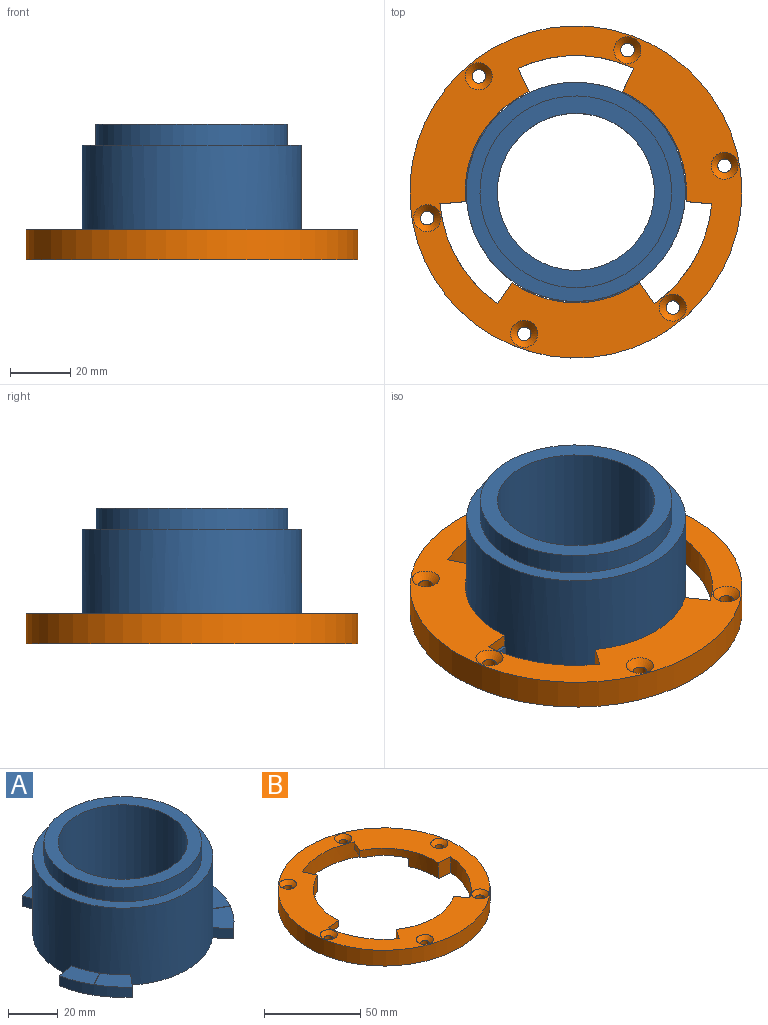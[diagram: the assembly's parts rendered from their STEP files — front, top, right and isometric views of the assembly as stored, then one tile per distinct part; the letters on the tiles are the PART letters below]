
ASSEMBLY  parts=2 mates=1
PART A: 24 faces, bbox 88.2x81.1x45 mm
  f0: cylinder r=36.3mm len=72.6mm, axis (0,0,-1), area 8278.7mm2, adj f4,f5,f9,f10,f11,f12,f13,f14
  f1: cylinder r=44.8mm len=26.54mm, axis (0,0,-1), area 160.6mm2, adj f4,f12,f14,f18,f19,f20
  f2: cylinder r=44.8mm len=30.65mm, axis (0,0,-1), area 160.6mm2, adj f4,f9,f11,f15,f16,f17
  f3: cylinder r=44.8mm len=26.54mm, axis (0,0,-1), area 160.6mm2, adj f4,f10,f13,f21,f22,f23
  f4: plane 88.24x81.1mm, normal (0,0,-1), area 2737.8mm2, adj f0,f1,f2,f3,f6,f9,f10,f11
  f5: plane 72.6x72.6mm, normal (0,0,1), area 972.7mm2, adj f0,f7
  f6: cylinder r=26mm len=52mm, axis (0,0,-1), area 7351.3mm2, adj f4,f8
  f7: cylinder r=31.75mm len=63.5mm, axis (0,0,-1), area 1396.4mm2, adj f5,f8
  f8: plane 63.5x63.5mm, normal (0,0,1), area 1043.2mm2, adj f6,f7
  f9: plane 7.99x5mm, normal (-0.94,-0.34,0), area 42.5mm2, adj f0,f2,f4,f15
  f10: plane 8.37x5mm, normal (-0.17,0.98,0), area 42.5mm2, adj f0,f3,f4,f22
  f11: plane 7.99x5mm, normal (0.94,-0.34,0), area 42.5mm2, adj f0,f2,f4,f16
  f12: plane 8.37x5mm, normal (0.17,0.98,0), area 42.5mm2, adj f0,f1,f4,f18
  f13: plane 6.51x5.46mm, normal (0.77,-0.64,0), area 42.5mm2, adj f0,f3,f4,f21
  f14: plane 6.51x5.46mm, normal (-0.77,-0.64,0), area 42.5mm2, adj f0,f1,f4,f19
  f15: plane 15.16x10.69mm, normal (-0.02,-0.01,1), area 118.9mm2, adj f0,f2,f9,f17
  f16: plane 15.16x10.69mm, normal (0.02,-0.01,1), area 118.9mm2, adj f0,f2,f11,f17
  f17: cylinder r=10mm len=8.5mm, axis (0,1,0.01), area 2.8mm2, adj f0,f2,f15,f16
  f18: plane 15.96x12.61mm, normal (0,0.02,1), area 118.9mm2, adj f0,f1,f12,f20
  f19: plane 16.03x15.39mm, normal (-0.01,-0.01,1), area 118.9mm2, adj f0,f1,f14,f20
  f20: cylinder r=10mm len=7.53mm, axis (-0.87,0.5,-0.01), area 2.8mm2, adj f0,f1,f18,f19
  f21: plane 16.03x15.39mm, normal (0.01,-0.01,1), area 118.9mm2, adj f0,f3,f13,f23
  f22: plane 15.96x12.61mm, normal (0,0.02,1), area 118.9mm2, adj f0,f3,f10,f23
  f23: cylinder r=10mm len=7.53mm, axis (0.87,0.5,-0.01), area 2.8mm2, adj f0,f3,f21,f22
PART B: 39 faces, bbox 110x110x10 mm
  f0: plane 110x110mm, normal (0,0,-1), area 3536.2mm2, adj f4,f5,f6,f8,f9,f10,f11,f12
  f1: plane 8.47x4mm, normal (0.09,-1,0), area 34mm2, adj f5,f7,f9,f26
  f2: plane 6.96x4.88mm, normal (0.82,0.57,0), area 34mm2, adj f6,f7,f13,f25
  f3: plane 7.7x4mm, normal (-0.91,0.42,0), area 34mm2, adj f4,f7,f11,f24
  f4: cylinder r=36.7mm len=36.46mm, axis (0,0,-1), area 311.4mm2, adj f0,f3,f7,f14,f15,f16,f17,f24
  f5: cylinder r=36.7mm len=36.46mm, axis (0,0,-1), area 311.4mm2, adj f0,f1,f7,f12,f21,f22,f23,f26
  f6: cylinder r=36.7mm len=42.1mm, axis (0,0,-1), area 311.4mm2, adj f0,f2,f7,f10,f18,f19,f20,f25
  f7: plane 110x110mm, normal (0,0,1), area 3982.4mm2, adj f1,f2,f3,f4,f5,f6,f8,f9
  f8: cylinder r=55mm len=110mm, axis (0,0,-1), area 3455.8mm2, adj f0,f7
  f9: cylinder r=45.2mm len=62.95mm, axis (0,0,1), area 563.8mm2, adj f0,f1,f7,f10,f21,f22,f23,f26
  f10: plane 10x6.96mm, normal (-0.82,0.57,0), area 85mm2, adj f0,f6,f7,f9
  f11: cylinder r=45.2mm len=60.07mm, axis (0,0,1), area 563.8mm2, adj f0,f3,f7,f12,f15,f16,f17,f24
  f12: plane 10x7.7mm, normal (0.91,0.42,0), area 85mm2, adj f0,f5,f7,f11
  f13: cylinder r=45.2mm len=48.97mm, axis (0,0,1), area 563.8mm2, adj f0,f2,f7,f14,f18,f19,f20,f25
  f14: plane 10x8.47mm, normal (-0.09,-1,0), area 85mm2, adj f0,f4,f7,f13
  f15: plane 14.31x13.95mm, normal (0.02,-0.01,-1), area 101.1mm2, adj f4,f11,f17,f24
  f16: plane 7.7x5.2mm, normal (-0.42,0.91,0), area 44.2mm2, adj f0,f4,f11,f17
  f17: plane 16.46x15.02mm, normal (-0.01,0.02,-1), area 121.5mm2, adj f4,f11,f15,f16
  f18: plane 14.43x12.29mm, normal (-0.01,-0.01,-1), area 101.1mm2, adj f6,f13,f20,f25
  f19: plane 8.47x5.2mm, normal (1,-0.09,0), area 44.2mm2, adj f0,f6,f13,f20
  f20: plane 15.64x9.75mm, normal (0.02,0,-1), area 121.5mm2, adj f6,f13,f18,f19
  f21: plane 13.25x9.75mm, normal (0,0.02,-1), area 101.1mm2, adj f5,f9,f23,f26
  f22: plane 6.96x5.2mm, normal (-0.57,-0.82,0), area 44.2mm2, adj f0,f5,f9,f23
  f23: plane 16.43x13.6mm, normal (-0.01,-0.01,-1), area 121.5mm2, adj f5,f9,f21,f22
  f24: plane 8.79x5.74mm, normal (-0.27,0.13,-0.95), area 21.4mm2, adj f3,f4,f11,f15
  f25: plane 8.29x6.89mm, normal (0.25,0.17,-0.95), area 21.4mm2, adj f2,f6,f13,f18
  f26: plane 8.61x3.14mm, normal (0.03,-0.3,-0.95), area 21.4mm2, adj f1,f5,f9,f21
  f27: cylinder r=2.25mm len=7.77mm, axis (0,0,1), area 109.8mm2, adj f0,f28
  f28: cone r=2.25mm half-angle=45deg, axis (0,0,1), area 66.7mm2, adj f7,f27
  f29: cylinder r=2.25mm len=7.77mm, axis (0,0,1), area 109.8mm2, adj f0,f30
  f30: cone r=2.25mm half-angle=45deg, axis (0,0,1), area 66.7mm2, adj f7,f29
  f31: cylinder r=2.25mm len=7.77mm, axis (0,0,1), area 109.8mm2, adj f0,f32
  f32: cone r=2.25mm half-angle=45deg, axis (0,0,1), area 66.7mm2, adj f7,f31
  f33: cylinder r=2.25mm len=7.77mm, axis (0,0,1), area 109.8mm2, adj f0,f34
  f34: cone r=2.25mm half-angle=45deg, axis (0,0,1), area 66.7mm2, adj f7,f33
  f35: cylinder r=2.25mm len=7.77mm, axis (0,0,1), area 109.8mm2, adj f0,f36
  f36: cone r=2.25mm half-angle=45deg, axis (0,0,1), area 66.7mm2, adj f7,f35
  f37: cylinder r=2.25mm len=7.77mm, axis (0,0,1), area 109.8mm2, adj f0,f38
  f38: cone r=2.25mm half-angle=45deg, axis (0,0,1), area 66.7mm2, adj f7,f37
PLACE A rot(axis=(0,0,-1),45deg) t=(0,0,-5)mm
PLACE B at identity fixed
MATE revolute A.f0 <-> B.f8  axis (0,0,-1) through (0,0,-5)mm
